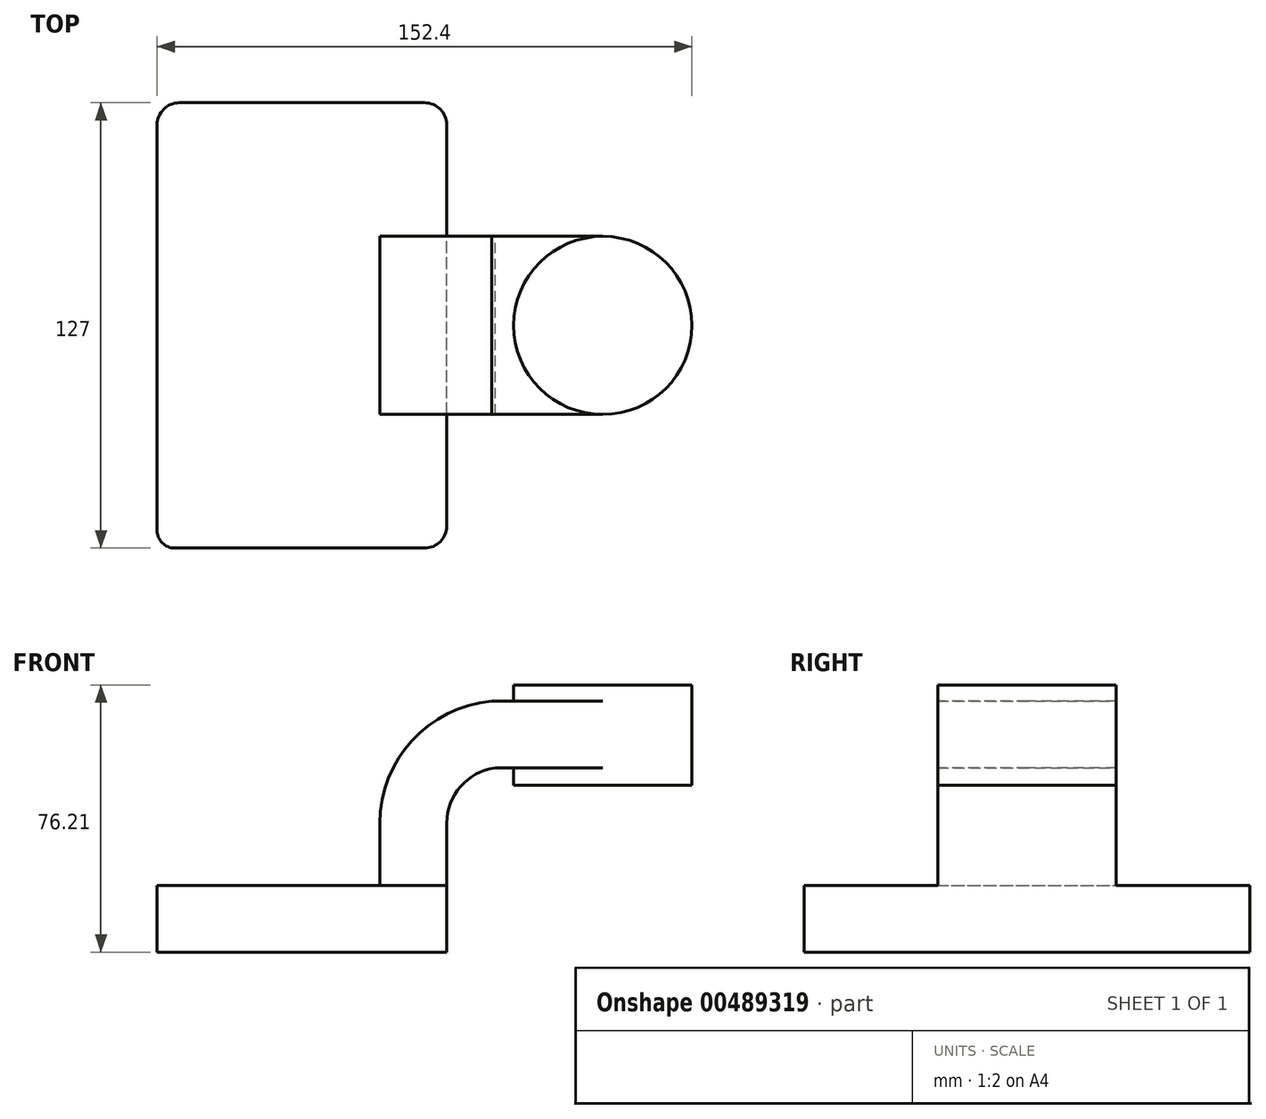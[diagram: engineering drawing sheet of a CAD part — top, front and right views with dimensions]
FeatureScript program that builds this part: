
annotation { "Feature Type Name" : "Feature", "Feature Type Description" : "" }
export const myFeature = defineFeature(function(context is Context, id is Id, definition is map)
    precondition{}
    {
        {
            var Q0;
            Q0=qCreatedBy(makeId("Front.planeOp"),FACE);
            var sketch = newSketch(context, id + "F0", { "sketchPlane" : qUnion([Q0])});
            skLineSegment(sketch, "E0.bottom", {"start": v(41.28, -9.52) * mm, "end": v(-41.28, -9.53) * mm});
            skLineSegment(sketch, "E0.top", {"start": v(41.28, 9.53) * mm, "end": v(-41.28, 9.52) * mm});
            skLineSegment(sketch, "E0.left", {"start": v(41.28, -9.52) * mm, "end": v(41.28, 9.53) * mm});
            skLineSegment(sketch, "E0.right", {"start": v(-41.28, -9.53) * mm, "end": v(-41.28, 9.52) * mm});
            skPoint(sketch, "E0.middle", {"position": v(0, 0) * mm});
            skLineSegment(sketch, "E1.bottom", {"start": v(60.32, 38.1) * mm, "end": v(111.12, 38.1) * mm});
            skLineSegment(sketch, "E1.top", {"start": v(60.32, 66.68) * mm, "end": v(111.12, 66.68) * mm});
            skLineSegment(sketch, "E1.left", {"start": v(60.32, 38.1) * mm, "end": v(60.32, 66.68) * mm});
            skLineSegment(sketch, "E1.right", {"start": v(111.12, 38.1) * mm, "end": v(111.12, 66.68) * mm});
            skPoint(sketch, "E1.middle", {"position": v(85.72, 52.39) * mm});
            skLineSegment(sketch, "E2", {"start": v(41.28, 9.53) * mm, "end": v(41.28, 27.24) * mm});
            skArc(sketch, "E3", {"start": v(41.28, 27.24) * mm, "mid": v(45.2, 37.69) * mm, "end": v(55.04, 42.97) * mm});
            skLineSegment(sketch, "E4", {"start": v(55.04, 42.97) * mm, "end": v(85.72, 42.97) * mm});
            skPoint(sketch, "E4.endSnap0", {"position": v(85.72, 38.1) * mm});
            skLineSegment(sketch, "E5.0", {"start": v(54.01, 62.02) * mm, "end": v(85.72, 62.02) * mm});
            skArc(sketch, "E5.1", {"start": v(22.23, 27.24) * mm, "mid": v(31.37, 50.8) * mm, "end": v(54.01, 62.02) * mm});
            skLineSegment(sketch, "E5.2", {"start": v(22.23, 9.53) * mm, "end": v(22.23, 27.24) * mm});
            skLineSegment(sketch, "E6", {"start": v(85.72, 38.1) * mm, "end": v(85.72, 66.68) * mm});
            skFitSpline(sketch, "E7", {"points": [v(-41.28, 9.52) * mm, v(54.01, 62.02) * mm], "startDerivative": vector(0.58, 67.53) * mm, "endDerivative": vector(128.53, 9.84) * mm});
            skSolve(sketch);
        }
        {
            var Q0;
            Q0=makeQuery(id+"F0.imprint","IMPRINT",FACE,{"disambiguationData":[TD([[makeQuery(id+"F0.imprint","IMPRINT",EDGE,{"derivedFrom":sQuery(id+"F0.wireOp",EDGE,"E0.bottom")}),-1.0]])]});
            extrude(context, id + "F1", {"entities" : qUnion([Q0]), "endBound" : BoundingType.SYMMETRIC, "depth" : 127 * mm});
        }
        {
            var Q0;
            {var subQ1=sQuery(id+"F0.wireOp",EDGE,"E2");Q0=makeQuery(id+"F0.imprint","IMPRINT",FACE,{"disambiguationData":[TD([[makeQuery(id+"F0.imprint","IMPRINT",EDGE,{"derivedFrom":subQ1}),1.0]])]});}
            extrude(context, id + "F2", {"entities" : qUnion([Q0]), "operationType" : NewBodyOperationType.ADD, "endBound" : BoundingType.SYMMETRIC, "depth" : 50.8 * mm});
        }
        {
            var Q0;
            Q0=makeQuery(id+"F0.imprint","IMPRINT",FACE,{"disambiguationData":[TD([[makeQuery(id+"F0.imprint","IMPRINT",EDGE,{"derivedFrom":sQuery(id+"F0.wireOp",EDGE,"E5.1")}),1.0]])]});
            extrude(context, id + "F3", {"entities" : qUnion([Q0]), "operationType" : NewBodyOperationType.ADD, "endBound" : BoundingType.SYMMETRIC, "depth" : 15.88 * mm});
        }
        {
            var Q0;
            {var subQ0=sQuery(id+"F0.wireOp",EDGE,"E4");var subQ1=sQuery(id+"F0.wireOp",EDGE,"E1.left");var subQ2=makeQuery(id+"F0.imprint","INTERSECT",VERTEX,{"derivedFrom":[subQ1,subQ0]});Q0=makeQuery(id+"F0.imprint","IMPRINT",FACE,{"disambiguationData":[TD([[makeQuery(id+"F0.imprint","IMPRINT",EDGE,{"disambiguationData":[TD([[subQ2,-1.0]])],"derivedFrom":subQ1}),-1.0]])]});}
            extrude(context, id + "F4", {"entities" : qUnion([Q0]), "operationType" : NewBodyOperationType.ADD, "endBound" : BoundingType.SYMMETRIC, "depth" : 50.8 * mm});
        }
        {
            var Q0;
            {var subQ0=sQuery(id+"F0.wireOp",EDGE,"E1.right");Q0=makeQuery(id+"F0.imprint","IMPRINT",FACE,{"disambiguationData":[TD([[makeQuery(id+"F0.imprint","IMPRINT",EDGE,{"derivedFrom":subQ0}),1.0]])]});}
            var Q1;
            Q1=sQuery(id+"F0.wireOp",EDGE,"E6");
            revolve(context, id + "F5", {"operationType" : NewBodyOperationType.ADD, "entities" : qUnion([Q0]), "axis" : qUnion([Q1]), "revolveType" : RevolveType.FULL});
        }
        {
            var Q0;
            Q0=makeQuery(id+"F1.opExtrude","CAP_EDGE",EDGE,{"disambiguationData":[OSD([sQuery(id+"F0.wireOp",EDGE,"E0.left")])],"isStart":true});
            var Q1;
            Q1=makeQuery(id+"F1.opExtrude","CAP_EDGE",EDGE,{"disambiguationData":[OSD([sQuery(id+"F0.wireOp",EDGE,"E0.right")])],"isStart":true});
            var Q2;
            Q2=makeQuery(id+"F1.opExtrude","CAP_EDGE",EDGE,{"disambiguationData":[OSD([sQuery(id+"F0.wireOp",EDGE,"E0.left")])],"isStart":false});
            fillet(context, id + "F6", {"entities" : qUnion([Q0, Q1, Q2]), "radius" : 6.35 * mm, "tangentPropagation" : true, "allowEdgeOverflow" : false});
        }
        {
            var Q0;
            Q0=makeQuery(id+"F1.opExtrude","CAP_EDGE",EDGE,{"disambiguationData":[OSD([sQuery(id+"F0.wireOp",EDGE,"E0.right")])],"isStart":false});
            fillet(context, id + "F7", {"entities" : qUnion([Q0]), "radius" : 5.08 * mm, "tangentPropagation" : true, "allowEdgeOverflow" : false});
        }
    });
